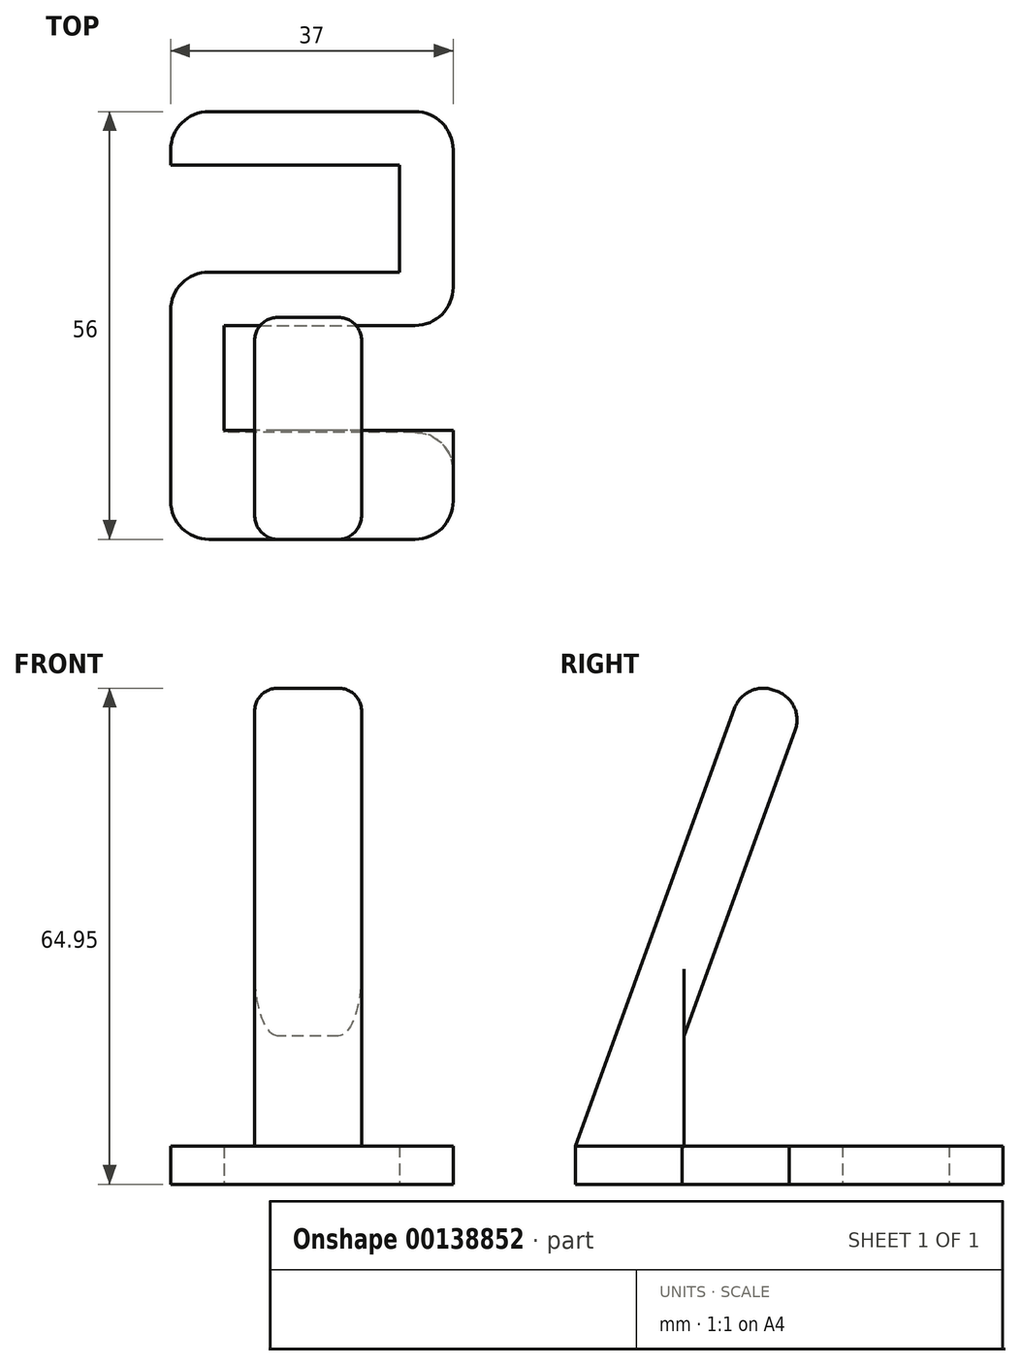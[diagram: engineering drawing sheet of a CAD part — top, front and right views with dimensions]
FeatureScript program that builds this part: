
annotation { "Feature Type Name" : "Feature", "Feature Type Description" : "" }
export const myFeature = defineFeature(function(context is Context, id is Id, definition is map)
    precondition{}
    {
        {
            var Q0;
            Q0=qCreatedBy(makeId("Top.planeOp"),FACE);
            var sketch = newSketch(context, id + "F0", { "sketchPlane" : qUnion([Q0])});
            skLineSegment(sketch, "E0", {"start": v(0, 0) * mm, "end": v(0, 35) * mm});
            skLineSegment(sketch, "E1", {"start": v(0, 35) * mm, "end": v(30, 35) * mm});
            skLineSegment(sketch, "E2", {"start": v(7, 28) * mm, "end": v(7, 14) * mm});
            skLineSegment(sketch, "E3", {"start": v(7, 14) * mm, "end": v(37, 14) * mm});
            skLineSegment(sketch, "E4", {"start": v(37, 14) * mm, "end": v(37, 0) * mm});
            skLineSegment(sketch, "E5", {"start": v(37, 0) * mm, "end": v(0, 0) * mm});
            skPoint(sketch, "E6.end.orphan", {"position": v(37, 24) * mm});
            skLineSegment(sketch, "E7", {"start": v(37, 35) * mm, "end": v(37, 56) * mm});
            skLineSegment(sketch, "E8", {"start": v(37, 56) * mm, "end": v(0, 56) * mm});
            skLineSegment(sketch, "E9", {"start": v(0, 56) * mm, "end": v(0, 49) * mm});
            skLineSegment(sketch, "E10", {"start": v(0, 49) * mm, "end": v(30, 49) * mm});
            skLineSegment(sketch, "E11", {"start": v(30, 49) * mm, "end": v(30, 35) * mm});
            skLineSegment(sketch, "E12", {"start": v(7, 28) * mm, "end": v(37, 28) * mm});
            skLineSegment(sketch, "E13", {"start": v(37, 28) * mm, "end": v(37, 35) * mm});
            skSolve(sketch);
        }
        {
            var Q0;
            Q0 = qSketchRegion(id + "F0", true);
            extrude(context, id + "F1", {"entities" : qUnion([Q0]), "depth" : 5 * mm});
        }
        {
            var Q0;
            Q0=qCreatedBy(makeId("Right.planeOp"),FACE);
            var sketch = newSketch(context, id + "F2", { "sketchPlane" : qUnion([Q0])});
            skLineSegment(sketch, "E14", {"start": v(0, 5) * mm, "end": v(22.23, 66.08) * mm});
            skLineSegment(sketch, "E15", {"start": v(22.23, 66.08) * mm, "end": v(30.18, 63.19) * mm});
            skLineSegment(sketch, "E16", {"start": v(30.18, 63.19) * mm, "end": v(14.25, 19.43) * mm});
            skLineSegment(sketch, "E17", {"start": v(9, 5) * mm, "end": v(0, 5) * mm});
            skLineSegment(sketch, "E18", {"start": v(14.25, 19.43) * mm, "end": v(14.25, 4.93) * mm});
            skLineSegment(sketch, "E19", {"start": v(14.25, 4.93) * mm, "end": v(9, 5) * mm});
            skSolve(sketch);
        }
        {
            var Q0;
            Q0 = qSketchRegion(id + "F2", true);
            extrude(context, id + "F3", {"entities" : qUnion([Q0]), "operationType" : NewBodyOperationType.ADD, "depth" : 37 * mm});
        }
        {
            var Q0;
            Q0=qCreatedBy(makeId("Front.planeOp"),FACE);
            var sketch = newSketch(context, id + "F4", { "sketchPlane" : qUnion([Q0])});
            skLineSegment(sketch, "E20.top", {"start": v(11, 66.08) * mm, "end": v(25, 66.08) * mm});
            skLineSegment(sketch, "E20.left", {"start": v(11, 5) * mm, "end": v(11, 66.08) * mm});
            skLineSegment(sketch, "E20.right", {"start": v(25, 5) * mm, "end": v(25, 66.08) * mm});
            skLineSegment(sketch, "E21", {"start": v(11, 5) * mm, "end": v(-15.33, 5) * mm});
            skLineSegment(sketch, "E22", {"start": v(-15.33, 5) * mm, "end": v(-15.33, 77.6) * mm});
            skLineSegment(sketch, "E23", {"start": v(-15.33, 77.6) * mm, "end": v(62, 77.6) * mm});
            skLineSegment(sketch, "E24", {"start": v(62, 77.6) * mm, "end": v(62, 5) * mm});
            skLineSegment(sketch, "E25", {"start": v(62, 5) * mm, "end": v(25, 5) * mm});
            skSolve(sketch);
        }
        {
            var Q0;
            Q0 = qSketchRegion(id + "F4", true);
            extrude(context, id + "F5", {"entities" : qUnion([Q0]), "operationType" : NewBodyOperationType.REMOVE, "oppositeDirection" : true, "depth" : 36.27 * mm});
        }
        {
            var Q0;
            Q0=makeQuery(id+"F3.opExtrude","SWEPT_EDGE",EDGE,{"disambiguationData":[OSD([sQuery(id+"F2.wireOp",EDGE,"E14"),sQuery(id+"F2.wireOp",EDGE,"E15")])]});
            var Q1;
            Q1=makeQuery(id+"F3.opExtrude","SWEPT_EDGE",EDGE,{"disambiguationData":[OSD([sQuery(id+"F2.wireOp",EDGE,"E15"),sQuery(id+"F2.wireOp",EDGE,"E16")])]});
            fillet(context, id + "F6", {"entities" : qUnion([Q0, Q1]), "radius" : 4 * mm, "tangentPropagation" : true, "allowEdgeOverflow" : false});
        }
        {
            var Q0;
            Q0=makeQuery(id+"F5.boolean.opBoolean","INTERSECT",EDGE,{"derivedFrom":[makeQuery(id+"F3.opExtrude","SWEPT_FACE",FACE,{"disambiguationData":[OSD([sQuery(id+"F2.wireOp",EDGE,"E16")])]}),makeQuery(id+"F5.opExtrude","SWEPT_FACE",FACE,{"disambiguationData":[OSD([sQuery(id+"F4.wireOp",EDGE,"E20.left")])]})]});
            var Q1;
            Q1=makeQuery(id+"F5.boolean.opBoolean","INTERSECT",EDGE,{"derivedFrom":[makeQuery(id+"F3.opExtrude","SWEPT_FACE",FACE,{"disambiguationData":[OSD([sQuery(id+"F2.wireOp",EDGE,"E14")])]}),makeQuery(id+"F5.opExtrude","SWEPT_FACE",FACE,{"disambiguationData":[OSD([sQuery(id+"F4.wireOp",EDGE,"E20.left")])]})]});
            var Q2;
            Q2=makeQuery(id+"F5.boolean.opBoolean","INTERSECT",EDGE,{"derivedFrom":[makeQuery(id+"F3.opExtrude","SWEPT_FACE",FACE,{"disambiguationData":[OSD([sQuery(id+"F2.wireOp",EDGE,"E16")])]}),makeQuery(id+"F5.opExtrude","SWEPT_FACE",FACE,{"disambiguationData":[OSD([sQuery(id+"F4.wireOp",EDGE,"E20.right")])]})]});
            var Q3;
            Q3=makeQuery(id+"F5.boolean.opBoolean","INTERSECT",EDGE,{"derivedFrom":[makeQuery(id+"F3.opExtrude","SWEPT_FACE",FACE,{"disambiguationData":[OSD([sQuery(id+"F2.wireOp",EDGE,"E14")])]}),makeQuery(id+"F5.opExtrude","SWEPT_FACE",FACE,{"disambiguationData":[OSD([sQuery(id+"F4.wireOp",EDGE,"E20.right")])]})]});
            fillet(context, id + "F7", {"entities" : qUnion([Q0, Q1, Q2, Q3]), "radius" : 3 * mm, "tangentPropagation" : true, "allowEdgeOverflow" : false});
        }
        {
            var Q0;
            Q0=makeQuery(id+"F1.opExtrude","SWEPT_EDGE",EDGE,{"disambiguationData":[OSD([sQuery(id+"F0.wireOp",EDGE,"E4"),sQuery(id+"F0.wireOp",EDGE,"E5")])]});
            var Q1;
            Q1=makeQuery(id+"F1.opExtrude","SWEPT_EDGE",EDGE,{"disambiguationData":[OSD([sQuery(id+"F0.wireOp",EDGE,"E12"),sQuery(id+"F0.wireOp",EDGE,"E13")])]});
            var Q2;
            Q2=makeQuery(id+"F1.opExtrude","SWEPT_EDGE",EDGE,{"disambiguationData":[OSD([sQuery(id+"F0.wireOp",EDGE,"E3"),sQuery(id+"F0.wireOp",EDGE,"E4")])]});
            var Q3;
            Q3=makeQuery(id+"F1.opExtrude","SWEPT_EDGE",EDGE,{"disambiguationData":[OSD([sQuery(id+"F0.wireOp",EDGE,"E0"),sQuery(id+"F0.wireOp",EDGE,"E5")])]});
            var Q4;
            Q4=makeQuery(id+"F1.opExtrude","SWEPT_EDGE",EDGE,{"disambiguationData":[OSD([sQuery(id+"F0.wireOp",EDGE,"E0"),sQuery(id+"F0.wireOp",EDGE,"E1")])]});
            var Q5;
            Q5=makeQuery(id+"F1.opExtrude","SWEPT_EDGE",EDGE,{"disambiguationData":[OSD([sQuery(id+"F0.wireOp",EDGE,"E8"),sQuery(id+"F0.wireOp",EDGE,"E9")])]});
            var Q6;
            Q6=makeQuery(id+"F1.opExtrude","SWEPT_EDGE",EDGE,{"disambiguationData":[OSD([sQuery(id+"F0.wireOp",EDGE,"E7"),sQuery(id+"F0.wireOp",EDGE,"E8")])]});
            fillet(context, id + "F8", {"entities" : qUnion([Q0, Q1, Q2, Q3, Q4, Q5, Q6]), "radius" : 5 * mm, "tangentPropagation" : true, "allowEdgeOverflow" : false});
        }
    });
